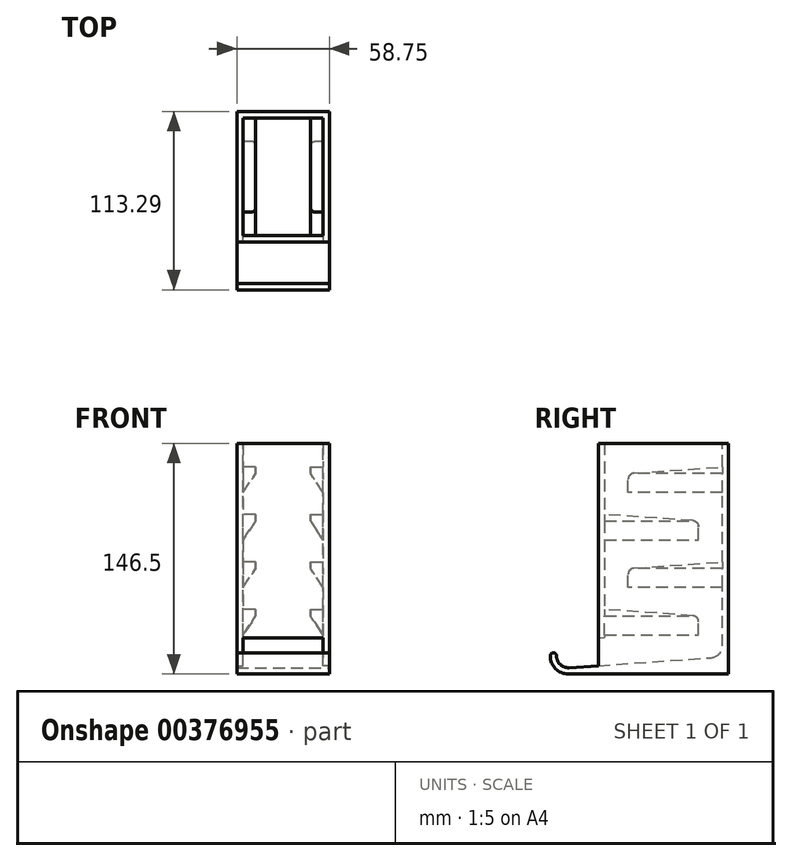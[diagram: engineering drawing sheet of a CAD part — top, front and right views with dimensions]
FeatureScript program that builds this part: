
annotation { "Feature Type Name" : "Feature", "Feature Type Description" : "" }
export const myFeature = defineFeature(function(context is Context, id is Id, definition is map)
    precondition{}
    {
        {
            var Q0;
            Q0=qCreatedBy(makeId("Right.planeOp"),FACE);
            var sketch = newSketch(context, id + "F0", { "sketchPlane" : qUnion([Q0])});
            skLineSegment(sketch, "E0", {"start": v(30.48, 146.5) * mm, "end": v(113.29, 146.5) * mm});
            skLineSegment(sketch, "E1", {"start": v(113.29, 146.5) * mm, "end": v(113.29, 0) * mm});
            skLineSegment(sketch, "E2", {"start": v(113.29, 0) * mm, "end": v(30.48, 0) * mm});
            skLineSegment(sketch, "E3", {"start": v(30.48, 0) * mm, "end": v(30.48, 146.5) * mm});
            skLineSegment(sketch, "E4", {"start": v(30.48, 0) * mm, "end": v(11.5, 0) * mm});
            skArc(sketch, "E5", {"start": v(11.5, 0) * mm, "mid": v(3.37, 3.37) * mm, "end": v(0, 11.5) * mm});
            skArc(sketch, "E6", {"start": v(4, 11.5) * mm, "mid": v(6.39, 6.01) * mm, "end": v(12.02, 4.02) * mm});
            skLineSegment(sketch, "E7", {"start": v(12.02, 4.02) * mm, "end": v(109.29, 10.82) * mm});
            skLineSegment(sketch, "E8", {"start": v(109.29, 10.82) * mm, "end": v(109.29, 54.98) * mm});
            skLineSegment(sketch, "E9", {"start": v(109.29, 54.98) * mm, "end": v(49.48, 54.98) * mm});
            skLineSegment(sketch, "E10", {"start": v(49.48, 66.98) * mm, "end": v(109.29, 71.16) * mm});
            skLineSegment(sketch, "E11", {"start": v(109.29, 71.16) * mm, "end": v(109.29, 115.32) * mm});
            skLineSegment(sketch, "E12", {"start": v(109.29, 115.32) * mm, "end": v(49.48, 115.32) * mm});
            skLineSegment(sketch, "E13", {"start": v(49.48, 127.32) * mm, "end": v(109.29, 131.5) * mm});
            skLineSegment(sketch, "E14", {"start": v(49.48, 115.32) * mm, "end": v(49.48, 127.32) * mm});
            skLineSegment(sketch, "E15", {"start": v(49.48, 54.98) * mm, "end": v(49.48, 66.98) * mm});
            skPoint(sketch, "E16", {"position": v(30.48, 5.3) * mm});
            skArc(sketch, "E17", {"start": v(0, 11.5) * mm, "mid": v(2, 13.5) * mm, "end": v(4, 11.5) * mm});
            skLineSegment(sketch, "E18", {"start": v(30.48, 22.85) * mm, "end": v(34.48, 23.13) * mm});
            skLineSegment(sketch, "E19", {"start": v(34.48, 23.13) * mm, "end": v(34.48, 24.8) * mm});
            skLineSegment(sketch, "E20", {"start": v(34.48, 24.8) * mm, "end": v(94.29, 24.8) * mm});
            skLineSegment(sketch, "E21", {"start": v(94.29, 24.8) * mm, "end": v(94.29, 36.8) * mm});
            skLineSegment(sketch, "E22", {"start": v(94.29, 36.8) * mm, "end": v(34.48, 40.99) * mm});
            skLineSegment(sketch, "E23", {"start": v(34.48, 40.99) * mm, "end": v(34.48, 85.15) * mm});
            skLineSegment(sketch, "E24", {"start": v(34.48, 85.15) * mm, "end": v(94.29, 85.15) * mm});
            skLineSegment(sketch, "E25", {"start": v(94.29, 85.15) * mm, "end": v(94.29, 97.15) * mm});
            skLineSegment(sketch, "E26", {"start": v(94.29, 97.15) * mm, "end": v(34.48, 101.33) * mm});
            skLineSegment(sketch, "E27", {"start": v(34.48, 101.33) * mm, "end": v(34.48, 146.5) * mm});
            skLineSegment(sketch, "E28", {"start": v(109.29, 131.5) * mm, "end": v(109.29, 146.5) * mm});
            skLineSegment(sketch, "E29", {"start": v(34.48, 40.99) * mm, "end": v(34.48, 24.8) * mm});
            skLineSegment(sketch, "E30", {"start": v(34.48, 101.33) * mm, "end": v(34.48, 85.15) * mm});
            skLineSegment(sketch, "E31", {"start": v(109.29, 71.16) * mm, "end": v(109.29, 54.98) * mm});
            skLineSegment(sketch, "E32", {"start": v(109.29, 131.5) * mm, "end": v(109.29, 115.32) * mm});
            skArc(sketch, "E33", {"start": v(30.48, 22.85) * mm, "mid": v(25.42, 10.02) * mm, "end": v(12.98, 4.09) * mm});
            skSolve(sketch);
        }
        {
            var Q0;
            {var subQ0=sQuery(id+"F0.wireOp",EDGE,"E18");Q0=makeQuery(id+"F0.imprint","IMPRINT",FACE,{"disambiguationData":[TD([[makeQuery(id+"F0.imprint","IMPRINT",EDGE,{"derivedFrom":subQ0}),1.0]])]});}
            var Q1;
            {var subQ7=sQuery(id+"F0.wireOp",EDGE,"E8");Q1=makeQuery(id+"F0.imprint","IMPRINT",FACE,{"disambiguationData":[TD([[makeQuery(id+"F0.imprint","IMPRINT",EDGE,{"derivedFrom":subQ7}),1.0]])]});}
            var Q2;
            Q2=makeQuery(id+"F0.imprint","IMPRINT",FACE,{"disambiguationData":[TD([[makeQuery(id+"F0.imprint","IMPRINT",EDGE,{"derivedFrom":sQuery(id+"F0.wireOp",EDGE,"E12")}),-1.0]])]});
            var Q3;
            Q3=makeQuery(id+"F0.imprint","IMPRINT",FACE,{"disambiguationData":[TD([[makeQuery(id+"F0.imprint","IMPRINT",EDGE,{"derivedFrom":sQuery(id+"F0.wireOp",EDGE,"E24")}),1.0]])]});
            var Q4;
            Q4=makeQuery(id+"F0.imprint","IMPRINT",FACE,{"disambiguationData":[TD([[makeQuery(id+"F0.imprint","IMPRINT",EDGE,{"derivedFrom":sQuery(id+"F0.wireOp",EDGE,"E9")}),-1.0]])]});
            var Q5;
            Q5=makeQuery(id+"F0.imprint","IMPRINT",FACE,{"disambiguationData":[TD([[makeQuery(id+"F0.imprint","IMPRINT",EDGE,{"derivedFrom":sQuery(id+"F0.wireOp",EDGE,"E20")}),1.0]])]});
            var Q6;
            {var subQ4=sQuery(id+"F0.wireOp",EDGE,"E1");Q6=makeQuery(id+"F0.imprint","IMPRINT",FACE,{"disambiguationData":[TD([[makeQuery(id+"F0.imprint","IMPRINT",EDGE,{"derivedFrom":subQ4}),-1.0]])]});}
            var Q7;
            {var subQ0=sQuery(id+"F0.wireOp",EDGE,"E4");Q7=makeQuery(id+"F0.imprint","IMPRINT",FACE,{"disambiguationData":[TD([[makeQuery(id+"F0.imprint","IMPRINT",EDGE,{"derivedFrom":subQ0}),-1.0]])]});}
            var Q8;
            {var subQ0=sQuery(id+"F0.wireOp",EDGE,"E33");Q8=makeQuery(id+"F0.imprint","IMPRINT",FACE,{"disambiguationData":[TD([[makeQuery(id+"F0.imprint","IMPRINT",EDGE,{"derivedFrom":subQ0}),1.0]])]});}
            extrude(context, id + "F1", {"entities" : qUnion([Q0, Q1, Q2, Q3, Q4, Q5, Q6, Q7, Q8]), "oppositeDirection" : true, "depth" : 4 * mm});
        }
        {
            var Q0;
            Q0=makeQuery(id+"F0.imprint","IMPRINT",FACE,{"disambiguationData":[TD([[makeQuery(id+"F0.imprint","IMPRINT",EDGE,{"derivedFrom":sQuery(id+"F0.wireOp",EDGE,"E12")}),-1.0]])]});
            var Q1;
            Q1=makeQuery(id+"F0.imprint","IMPRINT",FACE,{"disambiguationData":[TD([[makeQuery(id+"F0.imprint","IMPRINT",EDGE,{"derivedFrom":sQuery(id+"F0.wireOp",EDGE,"E24")}),1.0]])]});
            var Q2;
            Q2=makeQuery(id+"F0.imprint","IMPRINT",FACE,{"disambiguationData":[TD([[makeQuery(id+"F0.imprint","IMPRINT",EDGE,{"derivedFrom":sQuery(id+"F0.wireOp",EDGE,"E9")}),-1.0]])]});
            var Q3;
            Q3=makeQuery(id+"F0.imprint","IMPRINT",FACE,{"disambiguationData":[TD([[makeQuery(id+"F0.imprint","IMPRINT",EDGE,{"derivedFrom":sQuery(id+"F0.wireOp",EDGE,"E20")}),1.0]])]});
            extrude(context, id + "F2", {"entities" : qUnion([Q0, Q1, Q2, Q3]), "operationType" : NewBodyOperationType.ADD, "depth" : 8 * mm});
        }
        {
            var Q0;
            Q0=makeQuery(id+"F2.opExtrude","SWEPT_FACE",FACE,{"disambiguationData":[OSD([sQuery(id+"F0.wireOp",EDGE,"E14")])]});
            var sketch = newSketch(context, id + "F3", { "sketchPlane" : qUnion([Q0])});
            skLineSegment(sketch, "E34", {"start": v(8, 115.32) * mm, "end": v(0, 115.32) * mm});
            skLineSegment(sketch, "E35", {"start": v(0, 115.32) * mm, "end": v(8, 127.32) * mm});
            skSolve(sketch);
        }
        {
            var Q0;
            Q0=makeQuery(id+"F3.imprint","IMPRINT",FACE,{"disambiguationData":[TD([[makeQuery(id+"F3.imprint","IMPRINT",EDGE,{"derivedFrom":sQuery(id+"F3.wireOp",EDGE,"E34")}),-1.0]])]});
            extrude(context, id + "F4", {"entities" : qUnion([Q0]), "operationType" : NewBodyOperationType.REMOVE, "endBound" : BoundingType.UP_TO_NEXT, "oppositeDirection" : true, "depth" : 25 * mm});
        }
        {
            var Q0;
            Q0=makeQuery(id+"F2.opExtrude","SWEPT_FACE",FACE,{"disambiguationData":[OSD([sQuery(id+"F0.wireOp",EDGE,"E25")])]});
            var sketch = newSketch(context, id + "F5", { "sketchPlane" : qUnion([Q0])});
            skLineSegment(sketch, "E36", {"start": v(0, 85.15) * mm, "end": v(-8, 97.15) * mm});
            skLineSegment(sketch, "E37", {"start": v(-8, 97.15) * mm, "end": v(-8, 85.15) * mm});
            skLineSegment(sketch, "E38", {"start": v(-8, 85.15) * mm, "end": v(0, 85.15) * mm});
            skSolve(sketch);
        }
        {
            var Q0;
            Q0=makeQuery(id+"F5.imprint","IMPRINT",FACE,{"disambiguationData":[TD([[makeQuery(id+"F5.imprint","IMPRINT",EDGE,{"derivedFrom":sQuery(id+"F5.wireOp",EDGE,"E36")}),1.0]])]});
            extrude(context, id + "F6", {"entities" : qUnion([Q0]), "operationType" : NewBodyOperationType.REMOVE, "endBound" : BoundingType.UP_TO_NEXT, "oppositeDirection" : true, "depth" : 25 * mm});
        }
        {
            var Q0;
            Q0=makeQuery(id+"F2.opExtrude","SWEPT_FACE",FACE,{"disambiguationData":[OSD([sQuery(id+"F0.wireOp",EDGE,"E15")])]});
            var sketch = newSketch(context, id + "F7", { "sketchPlane" : qUnion([Q0])});
            skLineSegment(sketch, "E39", {"start": v(0, 54.98) * mm, "end": v(8, 66.98) * mm});
            skSolve(sketch);
        }
        {
            var Q0;
            Q0=makeQuery(id+"F7.imprint","IMPRINT",FACE,{"disambiguationData":[TD([[makeQuery(id+"F7.imprint","IMPRINT",EDGE,{"derivedFrom":sQuery(id+"F7.wireOp",EDGE,"E39")}),-1.0]])]});
            extrude(context, id + "F8", {"entities" : qUnion([Q0]), "operationType" : NewBodyOperationType.REMOVE, "endBound" : BoundingType.UP_TO_NEXT, "oppositeDirection" : true, "depth" : 25 * mm});
        }
        {
            var Q0;
            Q0=makeQuery(id+"F2.opExtrude","SWEPT_FACE",FACE,{"disambiguationData":[OSD([sQuery(id+"F0.wireOp",EDGE,"E21")])]});
            var sketch = newSketch(context, id + "F9", { "sketchPlane" : qUnion([Q0])});
            skLineSegment(sketch, "E40", {"start": v(-8, 36.8) * mm, "end": v(0, 24.8) * mm});
            skSolve(sketch);
        }
        {
            var Q0;
            Q0=makeQuery(id+"F9.imprint","IMPRINT",FACE,{"disambiguationData":[TD([[makeQuery(id+"F9.imprint","IMPRINT",EDGE,{"derivedFrom":sQuery(id+"F9.wireOp",EDGE,"E40")}),-1.0]])]});
            extrude(context, id + "F10", {"entities" : qUnion([Q0]), "operationType" : NewBodyOperationType.REMOVE, "endBound" : BoundingType.UP_TO_NEXT, "oppositeDirection" : true, "depth" : 25 * mm});
        }
        {
            var Q0;
            Q0=makeQuery(id+"F4.boolean.opBoolean","COPY",EDGE,{"derivedFrom":makeQuery(id+"F4.opExtrude","SWEPT_EDGE",EDGE,{"disambiguationData":[OSD([sQuery(id+"F0.wireOp",EDGE,"E13"),sQuery(id+"F0.wireOp",EDGE,"E14"),sQuery(id+"F3.wireOp",EDGE,"E35")])]})});
            var Q1;
            Q1=makeQuery(id+"F6.boolean.opBoolean","COPY",EDGE,{"derivedFrom":makeQuery(id+"F6.opExtrude","SWEPT_EDGE",EDGE,{"disambiguationData":[OSD([sQuery(id+"F0.wireOp",EDGE,"E25"),sQuery(id+"F0.wireOp",EDGE,"E26"),sQuery(id+"F5.wireOp",EDGE,"E36"),sQuery(id+"F5.wireOp",EDGE,"E37")])]})});
            var Q2;
            Q2=makeQuery(id+"F8.boolean.opBoolean","COPY",EDGE,{"derivedFrom":makeQuery(id+"F8.opExtrude","SWEPT_EDGE",EDGE,{"disambiguationData":[OSD([sQuery(id+"F0.wireOp",EDGE,"E10"),sQuery(id+"F0.wireOp",EDGE,"E15"),sQuery(id+"F7.wireOp",EDGE,"E39")])]})});
            var Q3;
            Q3=makeQuery(id+"F10.boolean.opBoolean","COPY",EDGE,{"derivedFrom":makeQuery(id+"F10.opExtrude","SWEPT_EDGE",EDGE,{"disambiguationData":[OSD([sQuery(id+"F0.wireOp",EDGE,"E21"),sQuery(id+"F0.wireOp",EDGE,"E22"),sQuery(id+"F9.wireOp",EDGE,"E40")])]})});
            var Q4;
            Q4=makeQuery(id+"F2.opExtrude","SWEPT_EDGE",EDGE,{"disambiguationData":[OSD([sQuery(id+"F0.wireOp",EDGE,"E10"),sQuery(id+"F0.wireOp",EDGE,"E15")])]});
            var Q5;
            Q5=makeQuery(id+"F2.opExtrude","SWEPT_EDGE",EDGE,{"disambiguationData":[OSD([sQuery(id+"F0.wireOp",EDGE,"E21"),sQuery(id+"F0.wireOp",EDGE,"E22")])]});
            var Q6;
            Q6=makeQuery(id+"F2.opExtrude","SWEPT_EDGE",EDGE,{"disambiguationData":[OSD([sQuery(id+"F0.wireOp",EDGE,"E25"),sQuery(id+"F0.wireOp",EDGE,"E26")])]});
            var Q7;
            Q7=makeQuery(id+"F2.opExtrude","SWEPT_EDGE",EDGE,{"disambiguationData":[OSD([sQuery(id+"F0.wireOp",EDGE,"E13"),sQuery(id+"F0.wireOp",EDGE,"E14")])]});
            fillet(context, id + "F11", {"entities" : qUnion([Q0, Q1, Q2, Q3, Q4, Q5, Q6, Q7]), "radius" : 4 * mm, "tangentPropagation" : true, "allowEdgeOverflow" : false});
        }
        {
            var Q0;
            Q0=makeQuery(id+"F1.opExtrude","SWEPT_BODY",BODY,{"disambiguationData":[OSD([sQuery(id+"F0.wireOp",EDGE,"E0"),sQuery(id+"F0.wireOp",EDGE,"E1"),sQuery(id+"F0.wireOp",EDGE,"E2"),sQuery(id+"F0.wireOp",EDGE,"E3"),sQuery(id+"F0.wireOp",EDGE,"E4"),sQuery(id+"F0.wireOp",EDGE,"E5"),sQuery(id+"F0.wireOp",EDGE,"E6"),sQuery(id+"F0.wireOp",EDGE,"E7"),sQuery(id+"F0.wireOp",EDGE,"E17")])]});
            var Q1;
            Q1=makeQuery(id+"F1.opExtrude","CAP_FACE",FACE,{"disambiguationData":[OSD([sQuery(id+"F0.wireOp",EDGE,"E0"),sQuery(id+"F0.wireOp",EDGE,"E1"),sQuery(id+"F0.wireOp",EDGE,"E2"),sQuery(id+"F0.wireOp",EDGE,"E3"),sQuery(id+"F0.wireOp",EDGE,"E4"),sQuery(id+"F0.wireOp",EDGE,"E5"),sQuery(id+"F0.wireOp",EDGE,"E6"),sQuery(id+"F0.wireOp",EDGE,"E7"),sQuery(id+"F0.wireOp",EDGE,"E17")])],"isStart":true});
            mirror(context, id + "F12", {"entities" : qUnion([Q0]), "mirrorPlane" : qUnion([Q1])});
        }
        {
            var Q0;
            Q0=makeQuery(id+"F12.opPattern","COPY",BODY,{"derivedFrom":makeQuery(id+"F1.opExtrude","SWEPT_BODY",BODY,{"disambiguationData":[OSD([sQuery(id+"F0.wireOp",EDGE,"E0"),sQuery(id+"F0.wireOp",EDGE,"E1"),sQuery(id+"F0.wireOp",EDGE,"E2"),sQuery(id+"F0.wireOp",EDGE,"E3"),sQuery(id+"F0.wireOp",EDGE,"E4"),sQuery(id+"F0.wireOp",EDGE,"E5"),sQuery(id+"F0.wireOp",EDGE,"E6"),sQuery(id+"F0.wireOp",EDGE,"E7"),sQuery(id+"F0.wireOp",EDGE,"E17")])]}),"instanceName":"1"});
            transform(context, id + "F13", {"entities" : qUnion([Q0]), "transformType" : TransformType.TRANSLATION_3D, "dx" : 50.75 * mm, "dy" : 0 * mm, "dz" : 0 * mm, "makeCopy" : false});
        }
        {
            var Q0;
            {var subQ0=sQuery(id+"F0.wireOp",EDGE,"E18");Q0=makeQuery(id+"F0.imprint","IMPRINT",FACE,{"disambiguationData":[TD([[makeQuery(id+"F0.imprint","IMPRINT",EDGE,{"derivedFrom":subQ0}),1.0]])]});}
            var Q1;
            {var subQ4=sQuery(id+"F0.wireOp",EDGE,"E1");Q1=makeQuery(id+"F0.imprint","IMPRINT",FACE,{"disambiguationData":[TD([[makeQuery(id+"F0.imprint","IMPRINT",EDGE,{"derivedFrom":subQ4}),-1.0]])]});}
            var Q2;
            {var subQ0=sQuery(id+"F0.wireOp",EDGE,"E4");Q2=makeQuery(id+"F0.imprint","IMPRINT",FACE,{"disambiguationData":[TD([[makeQuery(id+"F0.imprint","IMPRINT",EDGE,{"derivedFrom":subQ0}),-1.0]])]});}
            extrude(context, id + "F14", {"entities" : qUnion([Q0, Q1, Q2]), "operationType" : NewBodyOperationType.ADD, "endBound" : BoundingType.UP_TO_NEXT, "depth" : 25 * mm});
        }
        {
            var Q0;
            Q0=makeQuery(id+"F2.opExtrude","SWEPT_EDGE",EDGE,{"disambiguationData":[OSD([sQuery(id+"F0.wireOp",EDGE,"E13"),sQuery(id+"F0.wireOp",EDGE,"E28"),sQuery(id+"F0.wireOp",EDGE,"E32")])]});
            var Q1;
            Q1=makeQuery(id+"F2.opExtrude","SWEPT_EDGE",EDGE,{"disambiguationData":[OSD([sQuery(id+"F0.wireOp",EDGE,"E10"),sQuery(id+"F0.wireOp",EDGE,"E11"),sQuery(id+"F0.wireOp",EDGE,"E31")])]});
            var Q2;
            Q2=makeQuery(id+"F12.opPattern","COPY",EDGE,{"derivedFrom":makeQuery(id+"F2.opExtrude","SWEPT_EDGE",EDGE,{"disambiguationData":[OSD([sQuery(id+"F0.wireOp",EDGE,"E10"),sQuery(id+"F0.wireOp",EDGE,"E11"),sQuery(id+"F0.wireOp",EDGE,"E31")])]}),"instanceName":"1"});
            var Q3;
            Q3=makeQuery(id+"F12.opPattern","COPY",EDGE,{"derivedFrom":makeQuery(id+"F2.opExtrude","SWEPT_EDGE",EDGE,{"disambiguationData":[OSD([sQuery(id+"F0.wireOp",EDGE,"E13"),sQuery(id+"F0.wireOp",EDGE,"E28"),sQuery(id+"F0.wireOp",EDGE,"E32")])]}),"instanceName":"1"});
            var Q4;
            Q4=makeQuery(id+"F2.opExtrude","SWEPT_EDGE",EDGE,{"disambiguationData":[OSD([sQuery(id+"F0.wireOp",EDGE,"E22"),sQuery(id+"F0.wireOp",EDGE,"E23"),sQuery(id+"F0.wireOp",EDGE,"E29")])]});
            var Q5;
            Q5=makeQuery(id+"F2.opExtrude","SWEPT_EDGE",EDGE,{"disambiguationData":[OSD([sQuery(id+"F0.wireOp",EDGE,"E26"),sQuery(id+"F0.wireOp",EDGE,"E27"),sQuery(id+"F0.wireOp",EDGE,"E30")])]});
            var Q6;
            Q6=makeQuery(id+"F12.opPattern","COPY",EDGE,{"derivedFrom":makeQuery(id+"F2.opExtrude","SWEPT_EDGE",EDGE,{"disambiguationData":[OSD([sQuery(id+"F0.wireOp",EDGE,"E22"),sQuery(id+"F0.wireOp",EDGE,"E23"),sQuery(id+"F0.wireOp",EDGE,"E29")])]}),"instanceName":"1"});
            var Q7;
            Q7=makeQuery(id+"F12.opPattern","COPY",EDGE,{"derivedFrom":makeQuery(id+"F2.opExtrude","SWEPT_EDGE",EDGE,{"disambiguationData":[OSD([sQuery(id+"F0.wireOp",EDGE,"E26"),sQuery(id+"F0.wireOp",EDGE,"E27"),sQuery(id+"F0.wireOp",EDGE,"E30")])]}),"instanceName":"1"});
            var Q8;
            Q8=makeQuery(id+"F14.opExtrude","SWEPT_EDGE",EDGE,{"disambiguationData":[OSD([sQuery(id+"F0.wireOp",EDGE,"E7"),sQuery(id+"F0.wireOp",EDGE,"E8")])]});
            fillet(context, id + "F15", {"entities" : qUnion([Q0, Q1, Q2, Q3, Q4, Q5, Q6, Q7, Q8]), "radius" : 7.5 * mm, "tangentPropagation" : true, "allowEdgeOverflow" : false});
        }
    });
